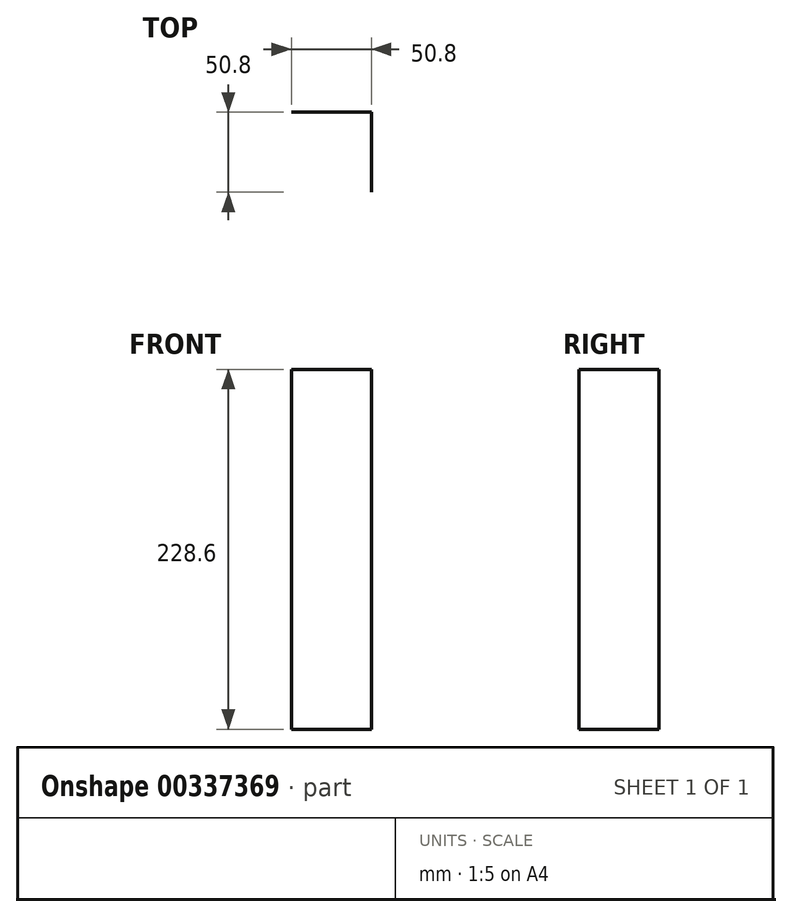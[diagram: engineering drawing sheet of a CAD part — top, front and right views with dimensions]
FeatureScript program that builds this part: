
annotation { "Feature Type Name" : "Feature", "Feature Type Description" : "" }
export const myFeature = defineFeature(function(context is Context, id is Id, definition is map)
    precondition{}
    {
        {
            var Q0;
            Q0=qCreatedBy(makeId("Top.planeOp"),FACE);
            var sketch = newSketch(context, id + "F0", { "sketchPlane" : qUnion([Q0])});
            skLineSegment(sketch, "E0", {"start": v(-149.1, 50.8) * mm, "end": v(-98.3, 50.8) * mm});
            skLineSegment(sketch, "E1", {"start": v(-98.3, 50.8) * mm, "end": v(-98.3, 0) * mm});
            skSolve(sketch);
        }
        {
            var Q0;
            Q0 = qSketchRegion(id + "F0", true);
            var Q1;
            Q1=sQuery(id+"F0.wireOp",EDGE,"E0");
            var Q2;
            Q2=sQuery(id+"F0.wireOp",EDGE,"E1");
            extrude(context, id + "F1", {"entities" : qUnion([Q0]), "bodyType" : ToolBodyType.SURFACE, "surfaceEntities" : qUnion([Q1, Q2]), "depth" : 228.6 * mm});
        }
    });
